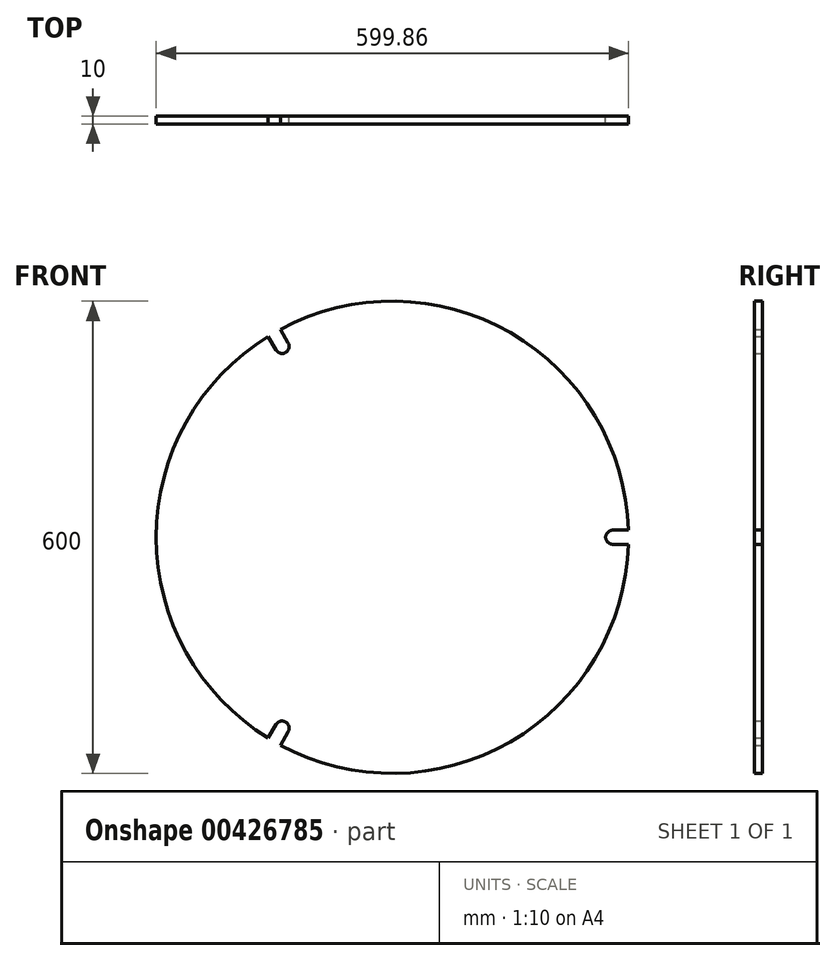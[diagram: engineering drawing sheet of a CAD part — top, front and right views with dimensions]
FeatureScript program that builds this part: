
annotation { "Feature Type Name" : "Feature", "Feature Type Description" : "" }
export const myFeature = defineFeature(function(context is Context, id is Id, definition is map)
    precondition{}
    {
        {
            var Q0;
            Q0=qCreatedBy(makeId("Front.planeOp"),FACE);
            var sketch = newSketch(context, id + "F0", { "sketchPlane" : qUnion([Q0])});
            skCircle(sketch, "E0", {"center": v(0, 0) * mm, "radius": 300 * mm});
            skCircle(sketch, "E1", {"center": v(0, 0) * mm, "radius": 254 * mm, "construction": true});
            skCircle(sketch, "E2.0", {"center": v(0, 0) * mm, "radius": 248 * mm, "construction": true});
            skLineSegment(sketch, "E3", {"start": v(0, 0) * mm, "end": v(-150, 259.8) * mm, "construction": true});
            skCircle(sketch, "E4", {"center": v(-140, 242.49) * mm, "radius": 9 * mm});
            skLineSegment(sketch, "E5", {"start": v(-132.2, 246.99) * mm, "end": v(-142.14, 264.2) * mm});
            skLineSegment(sketch, "E6", {"start": v(-147.8, 237.99) * mm, "end": v(-157.73, 255.2) * mm});
            skCircle(sketch, "E7", {"center": v(0, 0) * mm, "radius": 280 * mm, "construction": true});
            skLineSegment(sketch, "E8.1.0", {"start": v(-132.2, -246.99) * mm, "end": v(-142.14, -264.2) * mm});
            skCircle(sketch, "E8.1.1", {"center": v(-140, -242.49) * mm, "radius": 9 * mm});
            skLineSegment(sketch, "E8.1.2", {"start": v(-147.8, -237.99) * mm, "end": v(-157.73, -255.2) * mm});
            skLineSegment(sketch, "E8.2.0", {"start": v(280, 9) * mm, "end": v(299.86, 9) * mm});
            skCircle(sketch, "E8.2.1", {"center": v(280, 0) * mm, "radius": 9 * mm});
            skLineSegment(sketch, "E8.2.2", {"start": v(280, -9) * mm, "end": v(299.86, -9) * mm});
            skSolve(sketch);
        }
        {
            var Q0;
            Q0=makeQuery(id+"F0.imprint","IMPRINT",FACE,{"disambiguationData":[TD([[makeQuery(id+"F0.imprint","IMPRINT",EDGE,{"derivedFrom":sQuery(id+"F0.wireOp",EDGE,"E0")}),1.0]])]});
            extrude(context, id + "F1", {"entities" : qUnion([Q0]), "depth" : 10 * mm});
        }
    });
